# Revit family: Acoustical-EZPath-STI-EZ_Path_Series_33_Smoke_and_Acoustical_for_Walls
name_source: partatom
category: Specialty Equipment
units: mm (PartAtom-declared; Revit-internal decimal feet)

## family parameters
Always vertical = Yes
Cut with Voids When Loaded = No
Enable Cutting in Views = No
Host = Wall
Maintain Annotation Orientation = No
Part Type = Normal
Room Calculation Point = No
Round Connector Dimension = Use Diameter
Shared = No

## types (1)
- Acoustical-EZPath-STI-EZ_Path_Series_33_Smoke_and_Acoustical_for_Walls
    Assembly Code = C3030210
    Default Elevation = 0 "
    Device1 = Yes
    Device2 = Yes
    Device3 = Yes
    Device4 = Yes
    EZ-Path Center of Gang = 2.4375 "
    EZ-Path Corner = 0.5 "
    EZ-Path Device = Acoustic-STI-EZPath-EZPath_Smoke_and_Acoustic_Device_Blue
    EZ-Path Face Plate = 59.875 "
    Fire Rating = No Fire Rating
    Installation Instructions = https://files.stifirestop.com
    Manufacturer = Specified Technologies, Inc.
    Model = EZ-Path Series 33 Smoke & Acoustical Pathway
    Mouting Plate = Yes
    No. of Devices = 4
    Plate Edge Center Width = 12 "
    Plate Height = 5 "
    Plate Width = 24 "
    Product Data Sheet = https://files.stifirestop.com
    Product Page = https://www.stifirestop.com
    Retaining Plate = Acoustic-STI-EZPath-EZPath_Smoke_and_Acoustic_Plate
    Safety Data Sheet = https://files.stifirestop.com
    URL = https://www.stifirestop.com
    Wall Opening Center Width = 2 "
    Wall Opening Height = 4 "
    Wall Opening Width = 18.625 "
    center line 4 and 3 = 7.3125 "

## geometry (parser evidence)
native form markers: Blend x6, Sweep x3
no freeform markers — native parametric forms only
